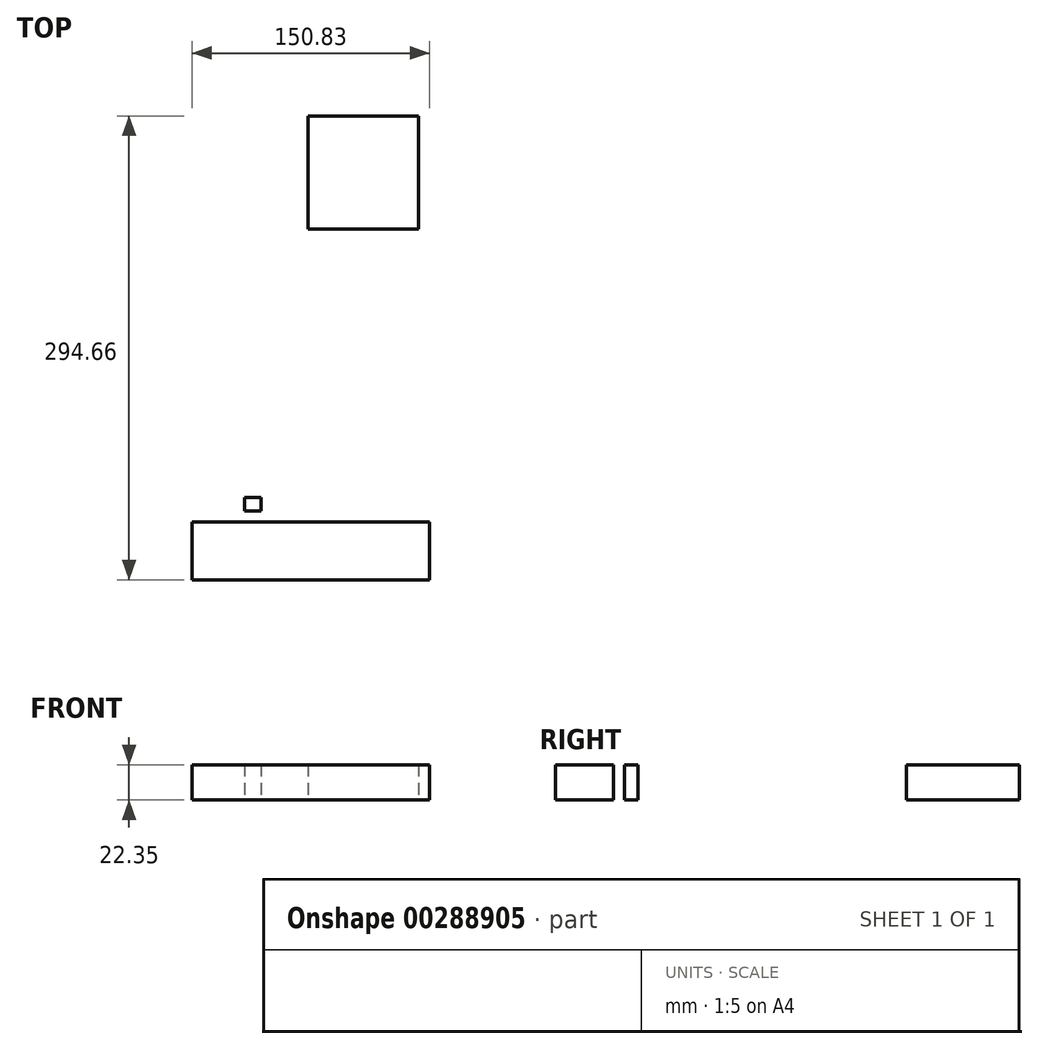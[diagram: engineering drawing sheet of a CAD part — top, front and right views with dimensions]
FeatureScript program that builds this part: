
annotation { "Feature Type Name" : "Feature", "Feature Type Description" : "" }
export const myFeature = defineFeature(function(context is Context, id is Id, definition is map)
    precondition{}
    {
        {
            var Q0;
            Q0=qCreatedBy(makeId("Top.planeOp"),FACE);
            var sketch = newSketch(context, id + "F0", { "sketchPlane" : qUnion([Q0])});
            skLineSegment(sketch, "E0.bottom", {"start": v(0, 0) * mm, "end": v(70.12, 0) * mm});
            skLineSegment(sketch, "E0.top", {"start": v(0, 71.83) * mm, "end": v(70.12, 71.83) * mm});
            skLineSegment(sketch, "E0.left", {"start": v(0, 0) * mm, "end": v(0, 71.83) * mm});
            skLineSegment(sketch, "E0.right", {"start": v(70.12, 0) * mm, "end": v(70.12, 71.83) * mm});
            skLineSegment(sketch, "E1.bottom", {"start": v(-40.37, -179) * mm, "end": v(-29.67, -179) * mm});
            skLineSegment(sketch, "E1.top", {"start": v(-40.37, -170.58) * mm, "end": v(-29.67, -170.58) * mm});
            skLineSegment(sketch, "E1.left", {"start": v(-40.37, -179) * mm, "end": v(-40.37, -170.58) * mm});
            skLineSegment(sketch, "E1.right", {"start": v(-29.67, -179) * mm, "end": v(-29.67, -170.58) * mm});
            skLineSegment(sketch, "E2.bottom", {"start": v(77.25, -222.83) * mm, "end": v(-73.58, -222.83) * mm});
            skLineSegment(sketch, "E2.top", {"start": v(77.25, -185.96) * mm, "end": v(-73.58, -185.96) * mm});
            skLineSegment(sketch, "E2.left", {"start": v(77.25, -222.83) * mm, "end": v(77.25, -185.96) * mm});
            skLineSegment(sketch, "E2.right", {"start": v(-73.58, -222.83) * mm, "end": v(-73.58, -185.96) * mm});
            skSolve(sketch);
        }
        {
            var Q0;
            Q0 = qSketchRegion(id + "F0", true);
            extrude(context, id + "F1", {"entities" : qUnion([Q0]), "depth" : 22.35 * mm});
        }
    });
